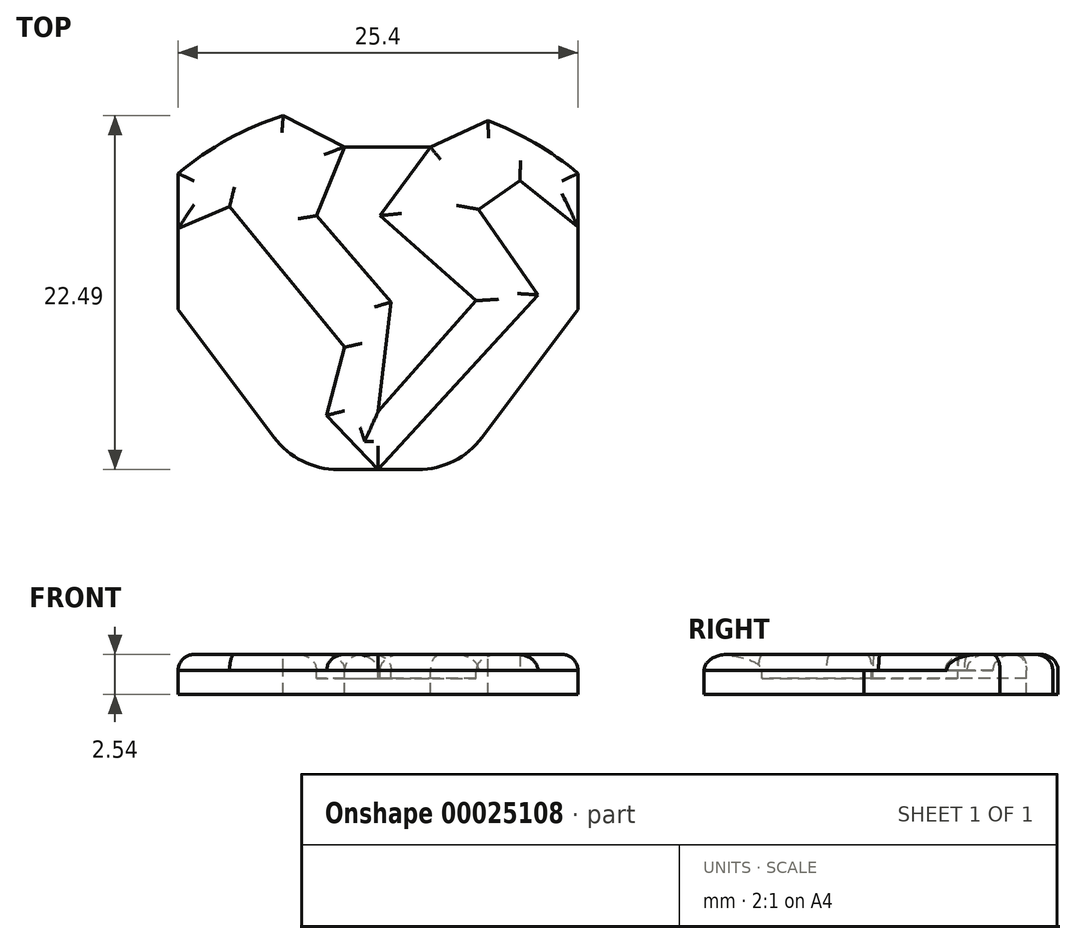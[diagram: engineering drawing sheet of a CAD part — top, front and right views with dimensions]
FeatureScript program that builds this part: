
annotation { "Feature Type Name" : "Feature", "Feature Type Description" : "" }
export const myFeature = defineFeature(function(context is Context, id is Id, definition is map)
    precondition{}
    {
        {
            var Q0;
            Q0=qCreatedBy(makeId("Top.planeOp"),FACE);
            var sketch = newSketch(context, id + "F0", { "sketchPlane" : qUnion([Q0])});
            skLineSegment(sketch, "E0.rect.bottom", {"start": v(-12.7, 12.7) * mm, "end": v(12.7, 12.7) * mm});
            skLineSegment(sketch, "E0.rect.top", {"start": v(-12.7, -12.7) * mm, "end": v(12.7, -12.7) * mm});
            skLineSegment(sketch, "E0.rect.left", {"start": v(-12.7, 12.7) * mm, "end": v(-12.7, -12.7) * mm});
            skLineSegment(sketch, "E0.rect.right", {"start": v(12.7, 12.7) * mm, "end": v(12.7, -12.7) * mm});
            skPoint(sketch, "E0.rect.middle", {"position": v(0, 0) * mm});
            skSolve(sketch);
        }
        {
            var Q0;
            Q0 = qSketchRegion(id + "F0", true);
            extrude(context, id + "F1", {"entities" : qUnion([Q0]), "depth" : 2.54 * mm});
        }
        {
            var Q0;
            Q0=makeQuery(id+"F1.opExtrude","CAP_FACE",FACE,{"disambiguationData":[OSD([sQuery(id+"F0.wireOp",EDGE,"E0.rect.bottom"),sQuery(id+"F0.wireOp",EDGE,"E0.rect.top"),sQuery(id+"F0.wireOp",EDGE,"E0.rect.left"),sQuery(id+"F0.wireOp",EDGE,"E0.rect.right")])],"isStart":false});
            var sketch = newSketch(context, id + "F2", { "sketchPlane" : qUnion([Q0])});
            skLineSegment(sketch, "E1", {"start": v(-12.7, 6.1) * mm, "end": v(12.7, 6.1) * mm});
            skArc(sketch, "E2", {"start": v(12.7, 6.1) * mm, "mid": v(0, 10.73) * mm, "end": v(-12.7, 6.1) * mm});
            skLineSegment(sketch, "E3.rect.bottom", {"start": v(-12.7, 12.7) * mm, "end": v(12.7, 12.7) * mm});
            skLineSegment(sketch, "E3.rect.top", {"start": v(-12.7, -12.7) * mm, "end": v(12.7, -12.7) * mm});
            skLineSegment(sketch, "E3.rect.left", {"start": v(-12.7, 12.7) * mm, "end": v(-12.7, -12.7) * mm});
            skLineSegment(sketch, "E3.rect.right", {"start": v(12.7, 12.7) * mm, "end": v(12.7, -12.7) * mm});
            skPoint(sketch, "E3.rect.middle", {"position": v(0, 0) * mm});
            skLineSegment(sketch, "E4", {"start": v(-6.02, 9.79) * mm, "end": v(-2.12, 7.8) * mm});
            skLineSegment(sketch, "E5", {"start": v(-2.12, 7.8) * mm, "end": v(-3.91, 3.42) * mm});
            skLineSegment(sketch, "E6", {"start": v(-3.91, 3.42) * mm, "end": v(0.84, -2.05) * mm});
            skLineSegment(sketch, "E7", {"start": v(0.84, -2.05) * mm, "end": v(0, -9.03) * mm});
            skLineSegment(sketch, "E8", {"start": v(0, -9.03) * mm, "end": v(6.22, -1.98) * mm});
            skLineSegment(sketch, "E9", {"start": v(6.22, -1.98) * mm, "end": v(0.1, 3.42) * mm});
            skLineSegment(sketch, "E10", {"start": v(0.1, 3.42) * mm, "end": v(3.32, 7.8) * mm});
            skLineSegment(sketch, "E11", {"start": v(3.32, 7.8) * mm, "end": v(6.98, 9.45) * mm});
            skSolve(sketch);
        }
        {
            var Q0;
            {var subQ4=sQuery(id+"F2.wireOp",EDGE,"E3.rect.bottom");Q0=makeQuery(id+"F2.imprint","IMPRINT",FACE,{"disambiguationData":[TD([[makeQuery(id+"F2.imprint","IMPRINT",EDGE,{"derivedFrom":subQ4}),-1.0]])]});}
            var Q1;
            {var subQ6=sQuery(id+"F2.wireOp",EDGE,"E4");Q1=makeQuery(id+"F2.imprint","IMPRINT",FACE,{"disambiguationData":[TD([[makeQuery(id+"F2.imprint","IMPRINT",EDGE,{"derivedFrom":subQ6}),1.0]])]});}
            var Q2;
            {var subQ4=sQuery(id+"F2.wireOp",EDGE,"E6");Q2=makeQuery(id+"F2.imprint","IMPRINT",FACE,{"disambiguationData":[TD([[makeQuery(id+"F2.imprint","IMPRINT",EDGE,{"derivedFrom":subQ4}),1.0]])]});}
            extrude(context, id + "F3", {"entities" : qUnion([Q0, Q1, Q2]), "operationType" : NewBodyOperationType.REMOVE, "oppositeDirection" : true, "depth" : 25.4 * mm});
        }
        {
            var Q0;
            Q0=makeQuery(id+"F1.opExtrude","CAP_FACE",FACE,{"disambiguationData":[OSD([sQuery(id+"F0.wireOp",EDGE,"E0.rect.bottom"),sQuery(id+"F0.wireOp",EDGE,"E0.rect.top"),sQuery(id+"F0.wireOp",EDGE,"E0.rect.left"),sQuery(id+"F0.wireOp",EDGE,"E0.rect.right")])],"isStart":false});
            var sketch = newSketch(context, id + "F4", { "sketchPlane" : qUnion([Q0])});
            skLineSegment(sketch, "E12", {"start": v(-12.7, 2.6) * mm, "end": v(-9.43, 4) * mm});
            skLineSegment(sketch, "E13", {"start": v(-9.43, 4) * mm, "end": v(-2.13, -4.93) * mm});
            skLineSegment(sketch, "E14", {"start": v(-2.13, -4.93) * mm, "end": v(-3.27, -9.27) * mm});
            skLineSegment(sketch, "E15", {"start": v(-3.27, -9.27) * mm, "end": v(0, -12.7) * mm});
            skLineSegment(sketch, "E16", {"start": v(0, -12.7) * mm, "end": v(10.16, -1.61) * mm});
            skLineSegment(sketch, "E17", {"start": v(10.16, -1.61) * mm, "end": v(6.38, 3.82) * mm});
            skLineSegment(sketch, "E18", {"start": v(6.38, 3.82) * mm, "end": v(9, 5.64) * mm});
            skLineSegment(sketch, "E19", {"start": v(9, 5.64) * mm, "end": v(12.7, 2.72) * mm});
            skLineSegment(sketch, "E20", {"start": v(12.7, 2.72) * mm, "end": v(12.7, -12.7) * mm});
            skLineSegment(sketch, "E21", {"start": v(12.7, -12.7) * mm, "end": v(-12.7, -12.7) * mm});
            skLineSegment(sketch, "E22", {"start": v(-12.7, -12.7) * mm, "end": v(-12.7, 2.6) * mm});
            skSolve(sketch);
        }
        {
            var Q0;
            Q0 = qSketchRegion(id + "F4", true);
            extrude(context, id + "F5", {"entities" : qUnion([Q0]), "operationType" : NewBodyOperationType.REMOVE, "oppositeDirection" : true, "depth" : 1.02 * mm});
        }
        {
            var Q0;
            Q0=makeQuery(id+"F1.opExtrude","SWEPT_EDGE",EDGE,{"disambiguationData":[OSD([sQuery(id+"F0.wireOp",EDGE,"E0.rect.top"),sQuery(id+"F0.wireOp",EDGE,"E0.rect.left")])]});
            var Q1;
            Q1=makeQuery(id+"F1.opExtrude","SWEPT_EDGE",EDGE,{"disambiguationData":[OSD([sQuery(id+"F0.wireOp",EDGE,"E0.rect.top"),sQuery(id+"F0.wireOp",EDGE,"E0.rect.right")])]});
            chamfer(context, id + "F6", {"entities" : qUnion([Q0, Q1]), "chamferType" : ChamferType.TWO_OFFSETS, "width1" : 7.62 * mm, "oppositeDirection" : false, "width2" : 10.16 * mm, "tangentPropagation" : true});
        }
        {
            var Q0;
            {var subQ0=sQuery(id+"F0.wireOp",EDGE,"E0.rect.top");Q0=makeQuery(id+"F6.opChamfer","BLEND_EDGE",EDGE,{"blendedFrom":[makeQuery(id+"F1.opExtrude","SWEPT_EDGE",EDGE,{"disambiguationData":[OSD([subQ0,sQuery(id+"F0.wireOp",EDGE,"E0.rect.left")])]}),makeQuery(id+"F1.opExtrude","SWEPT_FACE",FACE,{"disambiguationData":[OSD([subQ0])]})],"blendedInto":[makeQuery(id+"F1.opExtrude","SWEPT_FACE",FACE,{"disambiguationData":[OSD([subQ0])]})]});}
            var Q1;
            {var subQ0=sQuery(id+"F0.wireOp",EDGE,"E0.rect.top");Q1=makeQuery(id+"F6.opChamfer","BLEND_EDGE",EDGE,{"blendedFrom":[makeQuery(id+"F1.opExtrude","SWEPT_EDGE",EDGE,{"disambiguationData":[OSD([subQ0,sQuery(id+"F0.wireOp",EDGE,"E0.rect.right")])]}),makeQuery(id+"F1.opExtrude","SWEPT_FACE",FACE,{"disambiguationData":[OSD([subQ0])]})],"blendedInto":[makeQuery(id+"F1.opExtrude","SWEPT_FACE",FACE,{"disambiguationData":[OSD([subQ0])]})]});}
            fillet(context, id + "F7", {"entities" : qUnion([Q0, Q1]), "radius" : 5.08 * mm, "tangentPropagation" : true, "allowEdgeOverflow" : false});
        }
        {
            var Q0;
            Q0=makeQuery(id+"F3.boolean.opBoolean","COPY",EDGE,{"derivedFrom":makeQuery(id+"F3.opExtrude","CAP_EDGE",EDGE,{"disambiguationData":[OSD([sQuery(id+"F2.wireOp",EDGE,"E7")])],"isStart":true})});
            var Q1;
            Q1=makeQuery(id+"F3.boolean.opBoolean","COPY",EDGE,{"derivedFrom":makeQuery(id+"F3.opExtrude","CAP_EDGE",EDGE,{"disambiguationData":[OSD([sQuery(id+"F2.wireOp",EDGE,"E9")])],"isStart":true})});
            var Q2;
            Q2=makeQuery(id+"F1.opExtrude","CAP_FACE",FACE,{"disambiguationData":[OSD([sQuery(id+"F0.wireOp",EDGE,"E0.rect.bottom"),sQuery(id+"F0.wireOp",EDGE,"E0.rect.top"),sQuery(id+"F0.wireOp",EDGE,"E0.rect.left"),sQuery(id+"F0.wireOp",EDGE,"E0.rect.right")])],"isStart":false});
            fillet(context, id + "F8", {"entities" : qUnion([Q0, Q1, Q2]), "radius" : 1.02 * mm, "tangentPropagation" : true, "allowEdgeOverflow" : false});
        }
        {
            var Q0;
            Q0=makeQuery(id+"F1.opExtrude","CAP_FACE",FACE,{"disambiguationData":[OSD([sQuery(id+"F0.wireOp",EDGE,"E0.rect.bottom"),sQuery(id+"F0.wireOp",EDGE,"E0.rect.top"),sQuery(id+"F0.wireOp",EDGE,"E0.rect.left"),sQuery(id+"F0.wireOp",EDGE,"E0.rect.right")])],"isStart":true});
            var sketch = newSketch(context, id + "F9", { "sketchPlane" : qUnion([Q0])});
            skLineSegment(sketch, "E23", {"start": v(9.22, -1.48) * mm, "end": v(9.22, 3.79) * mm});
            skLineSegment(sketch, "E24", {"start": v(9.22, 3.79) * mm, "end": v(1.84, 10.06) * mm});
            skLineSegment(sketch, "E25", {"start": v(1.84, 10.06) * mm, "end": v(-2.98, 10.06) * mm});
            skLineSegment(sketch, "E26", {"start": v(-2.98, 10.06) * mm, "end": v(-9.77, -0.63) * mm});
            skLineSegment(sketch, "E27", {"start": v(-9.77, -0.63) * mm, "end": v(-5.68, -7.82) * mm});
            skLineSegment(sketch, "E28", {"start": v(-5.68, -7.82) * mm, "end": v(-2.12, -7.8) * mm});
            skLineSegment(sketch, "E29", {"start": v(-2.12, -7.8) * mm, "end": v(3.32, -7.8) * mm});
            skLineSegment(sketch, "E30", {"start": v(3.32, -7.8) * mm, "end": v(9.22, -1.48) * mm});
            skSolve(sketch);
        }
        {
            var Q0;
            Q0 = qSketchRegion(id + "F9", true);
            extrude(context, id + "F10", {"entities" : qUnion([Q0]), "operationType" : NewBodyOperationType.ADD, "oppositeDirection" : true, "depth" : 1.02 * mm});
        }
    });
